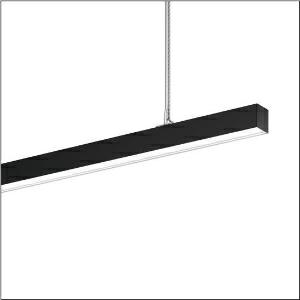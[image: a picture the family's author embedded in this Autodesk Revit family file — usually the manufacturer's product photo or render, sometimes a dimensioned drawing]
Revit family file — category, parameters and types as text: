
# Revit family: silica_r__21_51mx30da44bb_2b52
name_source: partatom
category: Lighting Fixtures
units: mm (PartAtom-declared; Revit-internal decimal feet)

## family parameters
Cut with Voids When Loaded = No
Host = Face
Light Source = No
Part Type = Normal
Room Calculation Point = No
Round Connector Dimension = Use Diameter
Shared = No

## types (1)
- --- (1 x LED, 4210 lm, 26 W, 4000K)
    Apparent Load = 26 VA
    CIE Flux Codes = 47 79 96 57 100
    Color Rendering = 80
    Color Temperature = 4000K
    Default Elevation = 1800 mm
    Description = Silica® 21, office luminaire, primary optical cover: cover, of PMMA, opal, light emission: direct/indirect distribution, primary light characteristic: symmetric, installation type: suspended mounting, LED, rated luminous flux: 4.210lm, luminous efficacy: 162lm/W, light colour: 840, colour temperature: 4000K, with terminal, 3+2-pole, max. 2.5mm², mains connection: 220..240V, AC, 50/60Hz, rated input power: 26W, luminaire housing, of aluminium, jet black (RAL 9005), length: 1.204mm, width: 53mm, height: 53mm, protection rating (complete): IP20, insulation class (complete): insulation class I (protective earthing), certification: CE, permissible operating ambient temperature: 0..+35°C, standard: EN 50419, packaging unit: 1 piece
    Height = 53 mm
    Lamp = 1 x LED
    Lamp Light Flux = 4210 lm
    Lamp Power = 26 W
    Lamp count = 1
    Length = 1204 mm
    Luminous efficacy = 162 lm/W
    Manufacturer = Siteco
    ModVariant = No
    Model = 51MX30DA44BB
    Mounting Place = Ceiling
    Mounting Type = Pendant
    Number of Poles = 1
    OnlyDefault = Yes
    Power Factor = 1
    Product Name = Silica® 21
    Product group = office luminaire | ceiling pendant
    ProductGroupID = 902
    Protection Class = Protection class I
    Protection Degree = IP 20
    RLX_Detail_Level = 1
    RLX_Emergency_Light_Flux = 0 lm
    RLX_Emergency_Type = 0
    RLX_Emergency_Type_DB = No
    RlxData = <blob elided: 25777 chars, md5=c9f1674e>
    Socket = socket
    Standby Power = 0 W
    System Light Flux = 4210 lm
    System Power = 26 W
    Type Comments = factory setting: luminous flux: 100 % | dim-lin: 254 | 218 mA
    Type Image = l_1313646.jpg
    URL = http://relux.com
    VarID = @adj_065547
    Voltage = 0 V
    Weight = 0.00 kg
    Width = 53 mm

## geometry (parser evidence)
native form markers: Blend x4, Sweep x13
no freeform markers — native parametric forms only
